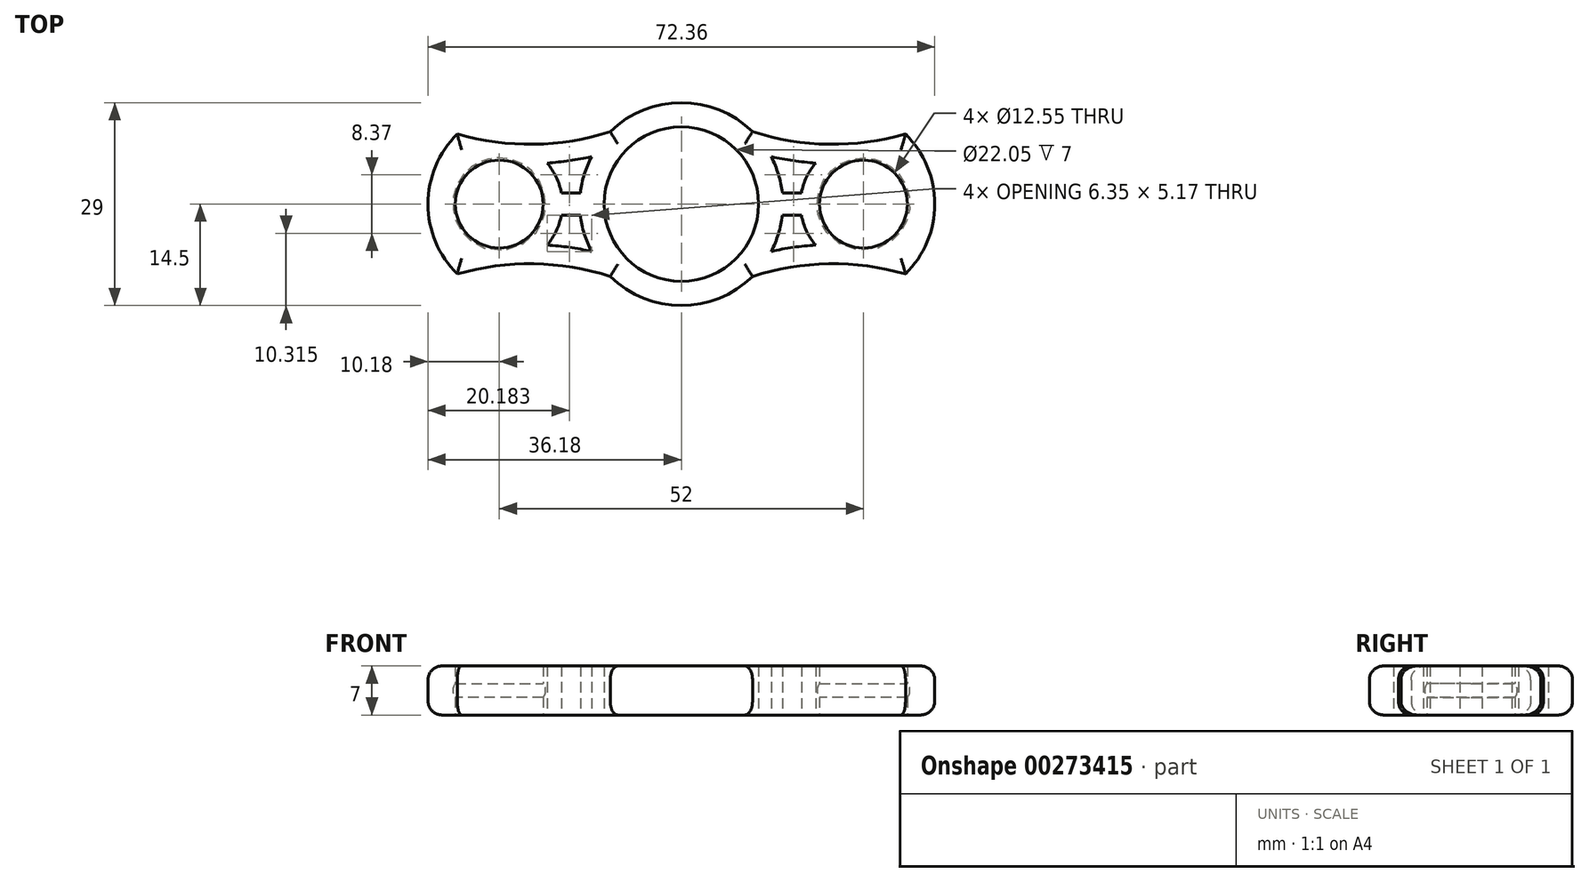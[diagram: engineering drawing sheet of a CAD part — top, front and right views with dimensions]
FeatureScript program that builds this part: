
annotation { "Feature Type Name" : "Feature", "Feature Type Description" : "" }
export const myFeature = defineFeature(function(context is Context, id is Id, definition is map)
    precondition{}
    {
        {
            var Q0;
            Q0=qCreatedBy(makeId("Top.planeOp"),FACE);
            var sketch = newSketch(context, id + "F0", { "sketchPlane" : qUnion([Q0])});
            skCircle(sketch, "E0", {"center": v(0, 0) * mm, "radius": 11.02 * mm});
            skLineSegment(sketch, "E1", {"start": v(26, 0) * mm, "end": v(0, 0) * mm, "construction": true});
            skArc(sketch, "E2", {"start": v(-10.16, -10.35) * mm, "mid": v(0, -14.5) * mm, "end": v(10.16, -10.35) * mm});
            skCircle(sketch, "E3", {"center": v(26, 0) * mm, "radius": 6.28 * mm});
            skLineSegment(sketch, "E4.MirrorCS", {"start": v(-26, 0) * mm, "end": v(0, 0) * mm, "construction": true});
            skCircle(sketch, "E5.MirrorC", {"center": v(-26, 0) * mm, "radius": 6.28 * mm});
            skArc(sketch, "E6", {"start": v(-10.16, -10.35) * mm, "mid": v(-21.05, -8.54) * mm, "end": v(-32, -10) * mm});
            skArc(sketch, "E7.MirrorCS", {"start": v(-10.16, 10.35) * mm, "mid": v(-21.05, 8.54) * mm, "end": v(-32, 10) * mm});
            skLineSegment(sketch, "E8", {"start": v(-32, 10) * mm, "end": v(-32, -10) * mm, "construction": true});
            skArc(sketch, "E9", {"start": v(-32, 10) * mm, "mid": v(-36.18, 0) * mm, "end": v(-32, -10) * mm});
            skArc(sketch, "E10.MirrorCS", {"start": v(10.16, 10.35) * mm, "mid": v(21.05, 8.54) * mm, "end": v(32, 10) * mm});
            skArc(sketch, "E11.MirrorCS", {"start": v(10.16, -10.35) * mm, "mid": v(21.05, -8.54) * mm, "end": v(32, -10) * mm});
            skArc(sketch, "E12.MirrorCS", {"start": v(32, 10) * mm, "mid": v(36.18, 0) * mm, "end": v(32, -10) * mm});
            skArc(sketch, "E13.trimOffspring", {"start": v(10.16, 10.35) * mm, "mid": v(0, 14.5) * mm, "end": v(-10.16, 10.35) * mm});
            skArc(sketch, "E14", {"start": v(-19.17, -5.86) * mm, "mid": v(-17.87, -3.87) * mm, "end": v(-17.14, -1.6) * mm});
            skArc(sketch, "E15", {"start": v(-12.82, 6.77) * mm, "mid": v(-13.86, 4.26) * mm, "end": v(-14.41, 1.6) * mm});
            skLineSegment(sketch, "E16", {"start": v(-17.14, 1.6) * mm, "end": v(-14.41, 1.6) * mm});
            skLineSegment(sketch, "E17.MirrorCS", {"start": v(-17.14, -1.6) * mm, "end": v(-14.41, -1.6) * mm});
            skArc(sketch, "E18.0", {"start": v(-12.82, 6.77) * mm, "mid": v(-15.98, 6.19) * mm, "end": v(-19.17, 5.86) * mm});
            skArc(sketch, "E19.trimOffspring", {"start": v(-31.6, 7.04) * mm, "mid": v(-32.18, 7.2) * mm, "end": v(-32.76, 7.36) * mm});
            skArc(sketch, "E20.trimOffspring", {"start": v(-31.6, 7.04) * mm, "mid": v(-31.8, 6.88) * mm, "end": v(-32, 6.7) * mm});
            skArc(sketch, "E21.MirrorCS", {"start": v(-12.82, -6.77) * mm, "mid": v(-15.98, -6.19) * mm, "end": v(-19.17, -5.86) * mm});
            skArc(sketch, "E22.trimOffspring", {"start": v(-17.14, 1.6) * mm, "mid": v(-17.87, 3.87) * mm, "end": v(-19.17, 5.86) * mm});
            skArc(sketch, "E23.trimOffspring", {"start": v(-14.41, -1.6) * mm, "mid": v(-13.86, -4.26) * mm, "end": v(-12.82, -6.77) * mm});
            skArc(sketch, "E24.MirrorCS", {"start": v(12.82, 6.77) * mm, "mid": v(15.98, 6.19) * mm, "end": v(19.17, 5.86) * mm});
            skArc(sketch, "E25.MirrorCS", {"start": v(17.14, 1.6) * mm, "mid": v(17.87, 3.87) * mm, "end": v(19.17, 5.86) * mm});
            skLineSegment(sketch, "E26.MirrorCS", {"start": v(17.14, 1.6) * mm, "end": v(14.41, 1.6) * mm});
            skArc(sketch, "E27.MirrorCS", {"start": v(12.82, 6.77) * mm, "mid": v(13.86, 4.26) * mm, "end": v(14.41, 1.6) * mm});
            skLineSegment(sketch, "E28.MirrorCS", {"start": v(17.14, -1.6) * mm, "end": v(14.41, -1.6) * mm});
            skArc(sketch, "E29.MirrorCS", {"start": v(19.17, -5.86) * mm, "mid": v(17.87, -3.87) * mm, "end": v(17.14, -1.6) * mm});
            skArc(sketch, "E30.MirrorCS", {"start": v(14.41, -1.6) * mm, "mid": v(13.86, -4.26) * mm, "end": v(12.82, -6.77) * mm});
            skArc(sketch, "E31.MirrorCS", {"start": v(12.82, -6.77) * mm, "mid": v(15.98, -6.19) * mm, "end": v(19.17, -5.86) * mm});
            skSolve(sketch);
        }
        {
            var Q0;
            Q0=makeQuery(id+"F0.imprint","IMPRINT",FACE,{"disambiguationData":[TD([[makeQuery(id+"F0.imprint","IMPRINT",EDGE,{"derivedFrom":sQuery(id+"F0.wireOp",EDGE,"E0")}),-1.0]])]});
            extrude(context, id + "F1", {"entities" : qUnion([Q0]), "depth" : 7 * mm});
        }
        {
            var Q0;
            Q0=makeQuery(id+"F1.opExtrude","CAP_EDGE",EDGE,{"disambiguationData":[OSD([sQuery(id+"F0.wireOp",EDGE,"E9")])],"isStart":false});
            var Q1;
            Q1=makeQuery(id+"F1.opExtrude","CAP_EDGE",EDGE,{"disambiguationData":[OSD([sQuery(id+"F0.wireOp",EDGE,"E2")])],"isStart":false});
            var Q2;
            Q2=makeQuery(id+"F1.opExtrude","CAP_EDGE",EDGE,{"disambiguationData":[OSD([sQuery(id+"F0.wireOp",EDGE,"E13.trimOffspring")])],"isStart":false});
            var Q3;
            Q3=makeQuery(id+"F1.opExtrude","CAP_EDGE",EDGE,{"disambiguationData":[OSD([sQuery(id+"F0.wireOp",EDGE,"E12.MirrorCS")])],"isStart":false});
            var Q4;
            Q4=makeQuery(id+"F1.opExtrude","CAP_EDGE",EDGE,{"disambiguationData":[OSD([sQuery(id+"F0.wireOp",EDGE,"E7.MirrorCS")])],"isStart":false});
            var Q5;
            Q5=makeQuery(id+"F1.opExtrude","CAP_EDGE",EDGE,{"disambiguationData":[OSD([sQuery(id+"F0.wireOp",EDGE,"E6")])],"isStart":false});
            var Q6;
            Q6=makeQuery(id+"F1.opExtrude","CAP_EDGE",EDGE,{"disambiguationData":[OSD([sQuery(id+"F0.wireOp",EDGE,"E11.MirrorCS")])],"isStart":false});
            var Q7;
            Q7=makeQuery(id+"F1.opExtrude","CAP_EDGE",EDGE,{"disambiguationData":[OSD([sQuery(id+"F0.wireOp",EDGE,"E10.MirrorCS")])],"isStart":false});
            var Q8;
            Q8=makeQuery(id+"F1.opExtrude","CAP_EDGE",EDGE,{"disambiguationData":[OSD([sQuery(id+"F0.wireOp",EDGE,"E7.MirrorCS")])],"isStart":true});
            var Q9;
            Q9=makeQuery(id+"F1.opExtrude","CAP_EDGE",EDGE,{"disambiguationData":[OSD([sQuery(id+"F0.wireOp",EDGE,"E9")])],"isStart":true});
            var Q10;
            Q10=makeQuery(id+"F1.opExtrude","CAP_EDGE",EDGE,{"disambiguationData":[OSD([sQuery(id+"F0.wireOp",EDGE,"E2")])],"isStart":true});
            var Q11;
            Q11=makeQuery(id+"F1.opExtrude","CAP_EDGE",EDGE,{"disambiguationData":[OSD([sQuery(id+"F0.wireOp",EDGE,"E13.trimOffspring")])],"isStart":true});
            var Q12;
            Q12=makeQuery(id+"F1.opExtrude","CAP_EDGE",EDGE,{"disambiguationData":[OSD([sQuery(id+"F0.wireOp",EDGE,"E10.MirrorCS")])],"isStart":true});
            var Q13;
            Q13=makeQuery(id+"F1.opExtrude","CAP_EDGE",EDGE,{"disambiguationData":[OSD([sQuery(id+"F0.wireOp",EDGE,"E12.MirrorCS")])],"isStart":true});
            var Q14;
            Q14=makeQuery(id+"F1.opExtrude","CAP_EDGE",EDGE,{"disambiguationData":[OSD([sQuery(id+"F0.wireOp",EDGE,"E11.MirrorCS")])],"isStart":true});
            var Q15;
            Q15=makeQuery(id+"F1.opExtrude","CAP_EDGE",EDGE,{"disambiguationData":[OSD([sQuery(id+"F0.wireOp",EDGE,"E6")])],"isStart":true});
            fillet(context, id + "F2", {"entities" : qUnion([Q0, Q1, Q2, Q3, Q4, Q5, Q6, Q7, Q8, Q9, Q10, Q11, Q12, Q13, Q14, Q15]), "radius" : 2 * mm, "tangentPropagation" : true, "allowEdgeOverflow" : false});
        }
        {
            var Q0;
            Q0=qCreatedBy(makeId("Front.planeOp"),FACE);
            var sketch = newSketch(context, id + "F3", { "sketchPlane" : qUnion([Q0])});
            skLineSegment(sketch, "E32", {"start": v(0, 0) * mm, "end": v(0, 3.5) * mm, "construction": true});
            skLineSegment(sketch, "E33", {"start": v(0, 0) * mm, "end": v(19.7, 0) * mm, "construction": true});
            skLineSegment(sketch, "E34", {"start": v(19.7, 0) * mm, "end": v(19.7, 7) * mm, "construction": true});
            skLineSegment(sketch, "E35", {"start": v(26, 7) * mm, "end": v(26, 0) * mm});
            skCircle(sketch, "E36", {"center": v(26, 3.5) * mm, "radius": 6.35 * mm, "construction": true});
            skCircle(sketch, "E37", {"center": v(20.9, 3.5) * mm, "radius": 1.52 * mm});
            skLineSegment(sketch, "E38", {"start": v(26, 3.5) * mm, "end": v(0, 3.5) * mm, "construction": true});
            skSolve(sketch);
        }
        {
            var Q0;
            Q0=makeQuery(id+"F3.imprint","IMPRINT",FACE,{"disambiguationData":[TD([[makeQuery(id+"F3.imprint","IMPRINT",EDGE,{"derivedFrom":sQuery(id+"F3.wireOp",EDGE,"E37")}),1.0]])]});
            var Q1;
            Q1=sQuery(id+"F3.wireOp",EDGE,"plMtQdIa-XCyh-ZVgV-Gdkr-hLrOiwfthBWz");
            var Q2;
            Q2=sQuery(id+"F3.wireOp",EDGE,"E35");
            revolve(context, id + "F4", {"operationType" : NewBodyOperationType.REMOVE, "entities" : qUnion([Q0]), "surfaceEntities" : qUnion([Q1]), "axis" : qUnion([Q2]), "revolveType" : RevolveType.FULL, "oppositeDirection" : true});
        }
        {
            var Q0;
            Q0=qCreatedBy(makeId("Front.planeOp"),FACE);
            var sketch = newSketch(context, id + "F5", { "sketchPlane" : qUnion([Q0])});
            skLineSegment(sketch, "E39", {"start": v(0, 0) * mm, "end": v(0, 3.5) * mm, "construction": true});
            skLineSegment(sketch, "E40", {"start": v(0, 3.5) * mm, "end": v(-26, 3.5) * mm, "construction": true});
            skCircle(sketch, "E41", {"center": v(-26, 3.5) * mm, "radius": 6.35 * mm, "construction": true});
            skLineSegment(sketch, "E42", {"start": v(-26, 7.8) * mm, "end": v(-26, -2.18) * mm});
            skCircle(sketch, "E43", {"center": v(-20.9, 3.5) * mm, "radius": 1.52 * mm});
            skSolve(sketch);
        }
        {
            var Q0;
            Q0=makeQuery(id+"F5.imprint","IMPRINT",FACE,{"disambiguationData":[TD([[makeQuery(id+"F5.imprint","IMPRINT",EDGE,{"derivedFrom":sQuery(id+"F5.wireOp",EDGE,"E43")}),1.0]])]});
            var Q1;
            Q1=sQuery(id+"F5.wireOp",EDGE,"E42");
            revolve(context, id + "F6", {"operationType" : NewBodyOperationType.REMOVE, "entities" : qUnion([Q0]), "axis" : qUnion([Q1]), "revolveType" : RevolveType.FULL});
        }
    });
